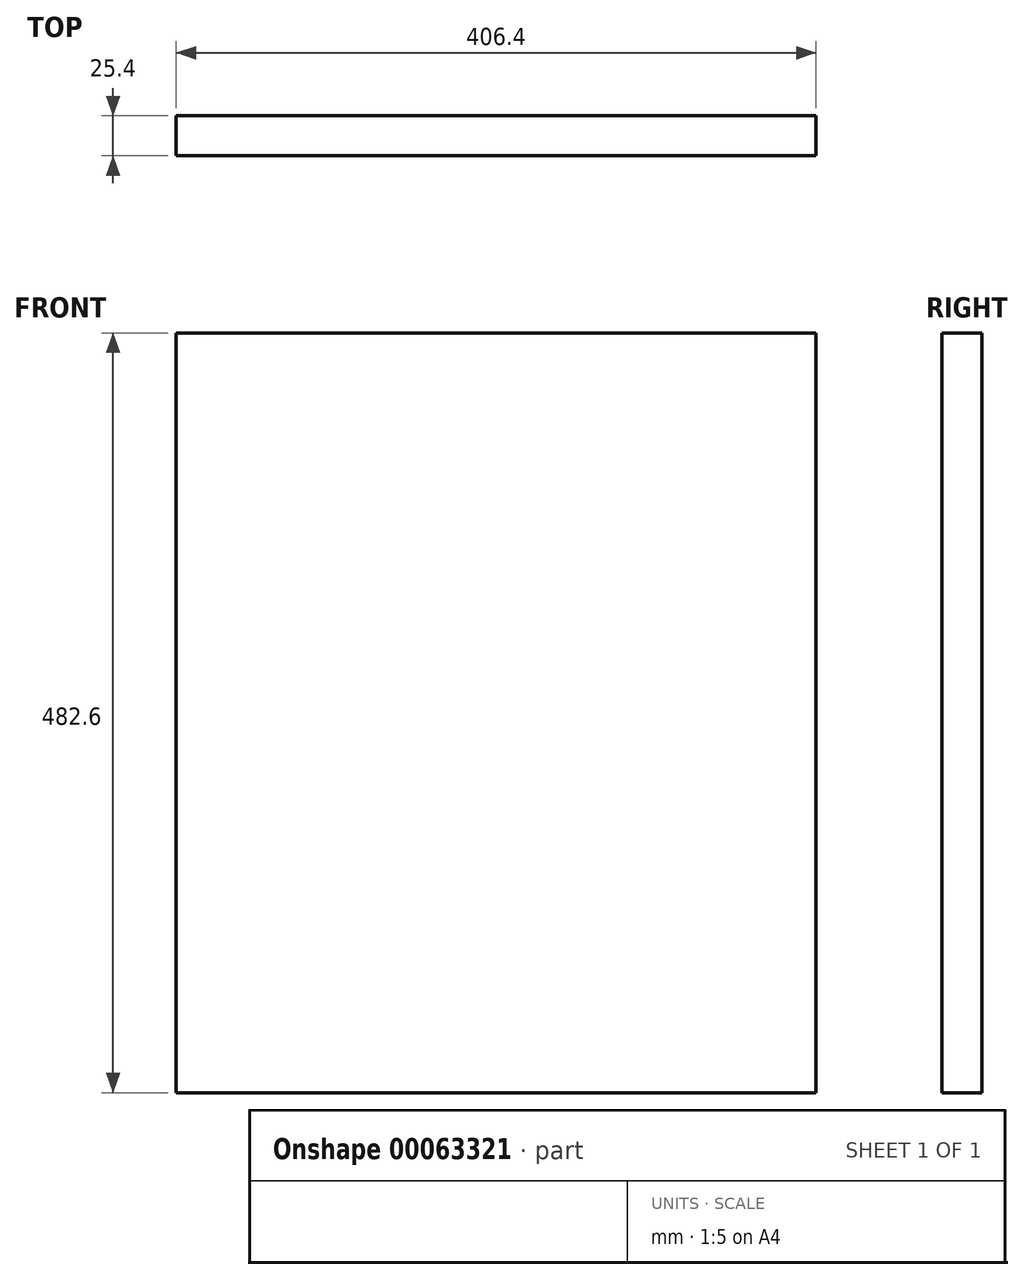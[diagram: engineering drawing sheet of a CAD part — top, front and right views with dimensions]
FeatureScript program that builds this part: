
annotation { "Feature Type Name" : "Feature", "Feature Type Description" : "" }
export const myFeature = defineFeature(function(context is Context, id is Id, definition is map)
    precondition{}
    {
        {
            var Q0;
            Q0=qCreatedBy(makeId("Front.planeOp"),FACE);
            var sketch = newSketch(context, id + "F0", { "sketchPlane" : qUnion([Q0])});
            skLineSegment(sketch, "E0.rect.bottom", {"start": v(-203.2, 241.3) * mm, "end": v(203.2, 241.3) * mm});
            skLineSegment(sketch, "E0.rect.top", {"start": v(-203.2, -241.3) * mm, "end": v(203.2, -241.3) * mm});
            skLineSegment(sketch, "E0.rect.left", {"start": v(-203.2, 241.3) * mm, "end": v(-203.2, -241.3) * mm});
            skLineSegment(sketch, "E0.rect.right", {"start": v(203.2, 241.3) * mm, "end": v(203.2, -241.3) * mm});
            skPoint(sketch, "E0.rect.middle", {"position": v(0, 0) * mm});
            skSolve(sketch);
        }
        {
            var Q0;
            Q0 = qSketchRegion(id + "F0", true);
            extrude(context, id + "F1", {"entities" : qUnion([Q0]), "depth" : 25.4 * mm});
        }
    });
